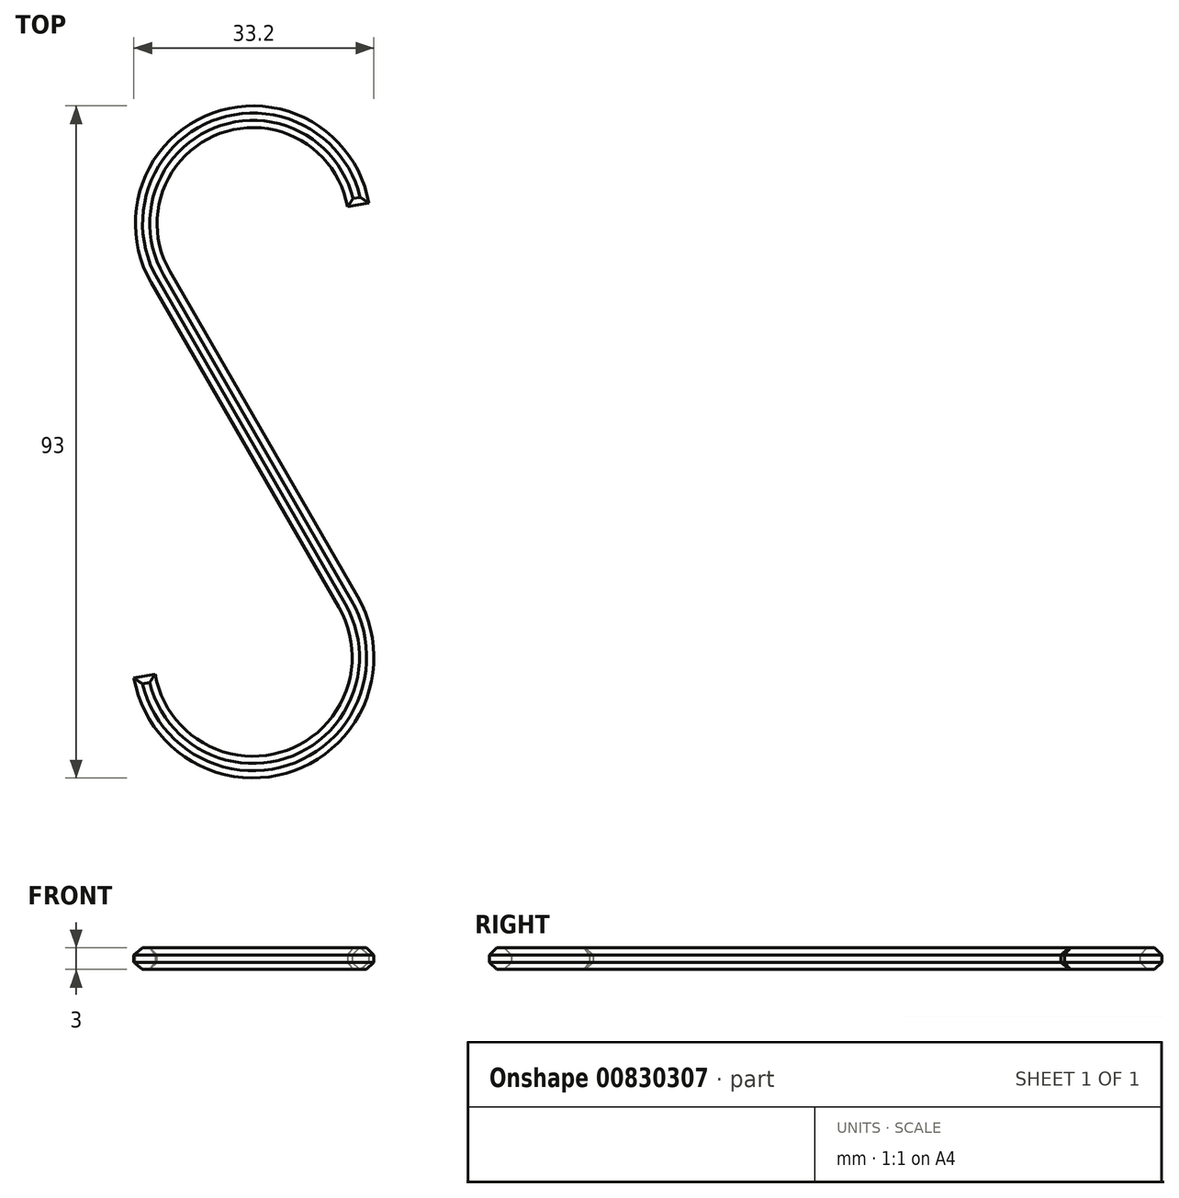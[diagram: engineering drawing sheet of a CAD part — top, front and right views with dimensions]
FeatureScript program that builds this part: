
annotation { "Feature Type Name" : "Feature", "Feature Type Description" : "" }
export const myFeature = defineFeature(function(context is Context, id is Id, definition is map)
    precondition{}
    {
        {
            var Q0;
            Q0=qCreatedBy(makeId("Top.planeOp"),FACE);
            var sketch = newSketch(context, id + "F0", { "sketchPlane" : qUnion([Q0])});
            skArc(sketch, "E0", {"start": v(14.77, 2.6) * mm, "mid": v(-5.13, 14.1) * mm, "end": v(-13, -7.5) * mm});
            skArc(sketch, "E1", {"start": v(-14.77, -62.6) * mm, "mid": v(5.13, -74.1) * mm, "end": v(13, -52.5) * mm});
            skLineSegment(sketch, "E2", {"start": v(-13, -7.5) * mm, "end": v(13, -52.5) * mm});
            skLineSegment(sketch, "E3", {"start": v(0, 0) * mm, "end": v(14.77, 2.6) * mm, "construction": true});
            skLineSegment(sketch, "E4", {"start": v(0, 0) * mm, "end": v(0, 15) * mm, "construction": true});
            skLineSegment(sketch, "E5", {"start": v(0, -60) * mm, "end": v(0, -75) * mm, "construction": true});
            skLineSegment(sketch, "E6", {"start": v(0, -60) * mm, "end": v(-14.77, -62.6) * mm, "construction": true});
            skSolve(sketch);
        }
        {
            var Q0;
            Q0=qCreatedBy(makeId("Front.planeOp"),FACE);
            var sketch = newSketch(context, id + "F1", { "sketchPlane" : qUnion([Q0])});
            skPoint(sketch, "E7.0", {"position": v(-14.77, 0) * mm});
            skLineSegment(sketch, "E8.bottom", {"start": v(-13.27, 1.5) * mm, "end": v(-16.27, 1.5) * mm});
            skLineSegment(sketch, "E8.top", {"start": v(-13.27, -1.5) * mm, "end": v(-16.27, -1.5) * mm});
            skLineSegment(sketch, "E8.left", {"start": v(-13.27, 1.5) * mm, "end": v(-13.27, -1.5) * mm});
            skLineSegment(sketch, "E8.right", {"start": v(-16.27, 1.5) * mm, "end": v(-16.27, -1.5) * mm});
            skSolve(sketch);
        }
        {
            var Q0;
            Q0=makeQuery(id+"F1.imprint","IMPRINT",FACE,{"disambiguationData":[TD([[makeQuery(id+"F1.imprint","IMPRINT",EDGE,{"derivedFrom":sQuery(id+"F1.wireOp",EDGE,"E8.bottom")}),1.0]])]});
            var Q1;
            Q1=sQuery(id+"F0.wireOp",EDGE,"E0");
            var Q2;
            Q2=sQuery(id+"F0.wireOp",EDGE,"E2");
            var Q3;
            Q3=sQuery(id+"F0.wireOp",EDGE,"E1");
            sweep(context, id + "F2", {"profiles" : qUnion([Q0]), "path" : qUnion([Q1, Q2, Q3])});
        }
        {
            var Q0;
            Q0=makeQuery(id+"F2.opSweep","SWEPT_FACE",FACE,{"disambiguationData":[OSD([sQuery(id+"F0.wireOp",EDGE,"E0"),sQuery(id+"F1.wireOp",EDGE,"E8.bottom")])]});
            var Q1;
            Q1=makeQuery(id+"F2.opSweep","SWEPT_FACE",FACE,{"disambiguationData":[OSD([sQuery(id+"F0.wireOp",EDGE,"E0"),sQuery(id+"F1.wireOp",EDGE,"E8.top")])]});
            chamfer(context, id + "F3", {"entities" : qUnion([Q0, Q1]), "width" : 1 * mm, "tangentPropagation" : true});
        }
    });
